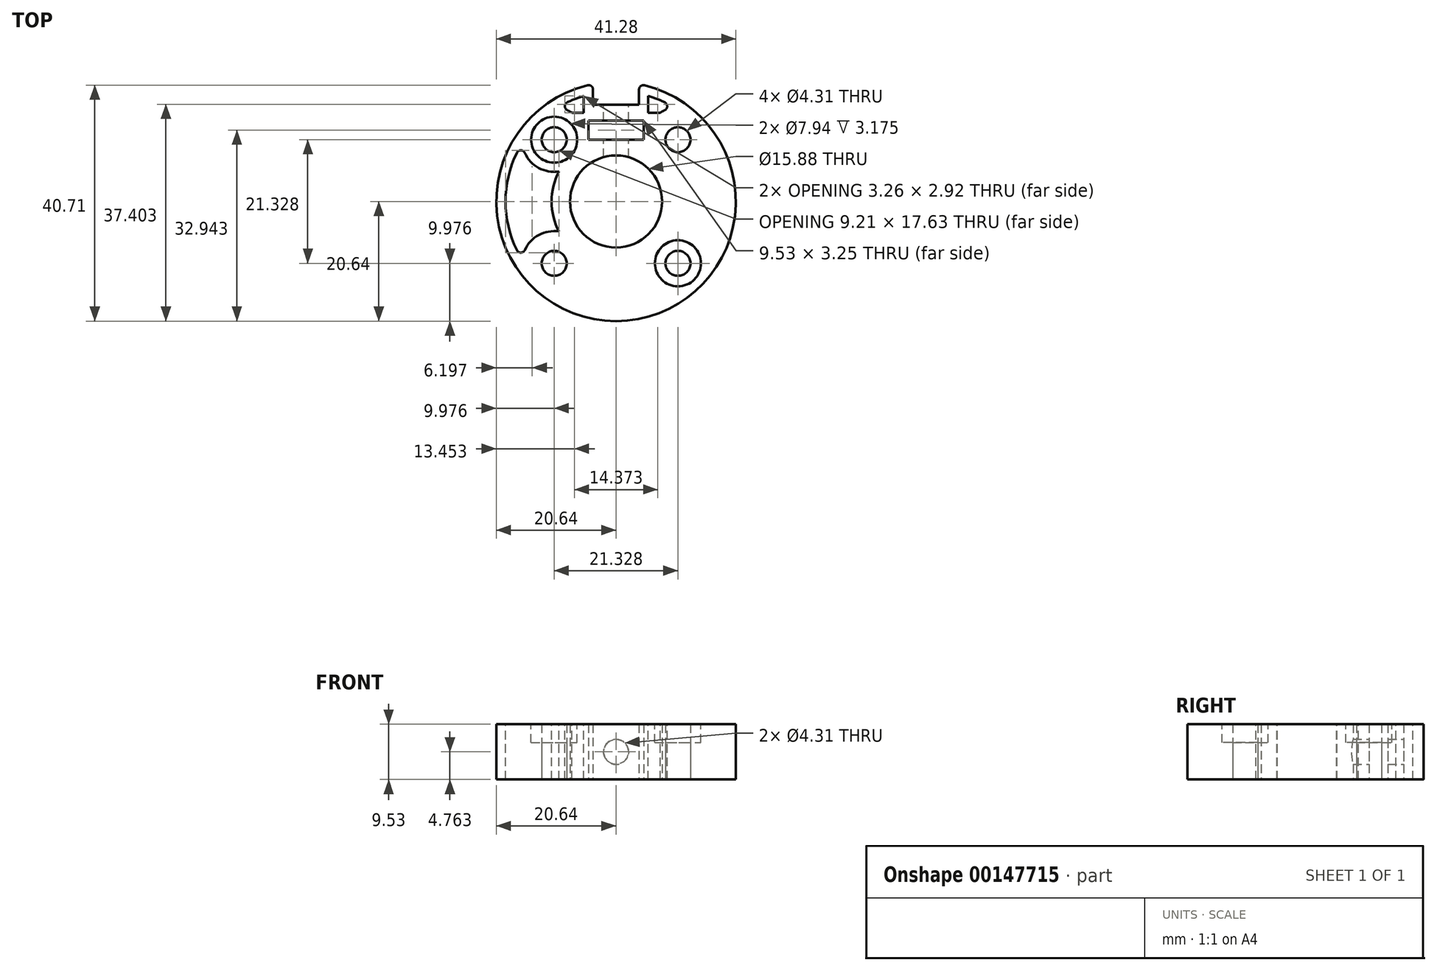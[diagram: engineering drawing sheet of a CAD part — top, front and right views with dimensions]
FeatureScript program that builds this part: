
annotation { "Feature Type Name" : "Feature", "Feature Type Description" : "" }
export const myFeature = defineFeature(function(context is Context, id is Id, definition is map)
    precondition{}
    {
        {
            var Q0;
            Q0=qCreatedBy(makeId("Top.planeOp"),FACE);
            var sketch = newSketch(context, id + "F0", { "sketchPlane" : qUnion([Q0])});
            skLineSegment(sketch, "E0.bottom", {"start": v(10.66, 10.66) * mm, "end": v(-10.66, 10.66) * mm, "construction": true});
            skLineSegment(sketch, "E0.top", {"start": v(10.66, -10.66) * mm, "end": v(-10.66, -10.66) * mm, "construction": true});
            skLineSegment(sketch, "E0.left", {"start": v(10.66, 10.66) * mm, "end": v(10.66, -10.66) * mm, "construction": true});
            skLineSegment(sketch, "E0.right", {"start": v(-10.66, 10.66) * mm, "end": v(-10.66, -10.66) * mm, "construction": true});
            skPoint(sketch, "E0.middle", {"position": v(0, 0) * mm});
            skCircle(sketch, "E1", {"center": v(-10.66, 10.66) * mm, "radius": 5.56 * mm, "construction": true});
            skLineSegment(sketch, "E2", {"start": v(0, 13.93) * mm, "end": v(0, 16.67) * mm});
            skLineSegment(sketch, "E3.bottom", {"start": v(-3.97, 20.25) * mm, "end": v(3.97, 20.25) * mm, "construction": true});
            skLineSegment(sketch, "E3.top", {"start": v(-3.97, 16.67) * mm, "end": v(3.97, 16.67) * mm});
            skLineSegment(sketch, "E3.left", {"start": v(-3.97, 20.25) * mm, "end": v(-3.97, 16.67) * mm});
            skLineSegment(sketch, "E3.right", {"start": v(3.97, 20.25) * mm, "end": v(3.97, 16.67) * mm});
            skArc(sketch, "E4", {"start": v(-3.97, 20.25) * mm, "mid": v(0, -20.64) * mm, "end": v(3.97, 20.25) * mm});
            skCircle(sketch, "E5", {"center": v(-10.66, 10.66) * mm, "radius": 2.15 * mm});
            skCircle(sketch, "E6", {"center": v(-10.66, -10.66) * mm, "radius": 2.15 * mm});
            skCircle(sketch, "E7", {"center": v(10.66, -10.66) * mm, "radius": 2.15 * mm});
            skCircle(sketch, "E8", {"center": v(10.66, 10.66) * mm, "radius": 2.15 * mm});
            skLineSegment(sketch, "E9.bottom", {"start": v(-4.76, 13.93) * mm, "end": v(4.76, 13.93) * mm});
            skLineSegment(sketch, "E9.top", {"start": v(-4.76, 10.68) * mm, "end": v(4.76, 10.68) * mm});
            skLineSegment(sketch, "E9.left", {"start": v(-4.76, 13.93) * mm, "end": v(-4.76, 10.68) * mm});
            skLineSegment(sketch, "E9.right", {"start": v(4.76, 13.93) * mm, "end": v(4.76, 10.68) * mm});
            skCircle(sketch, "E10", {"center": v(0, 0) * mm, "radius": 7.94 * mm});
            skCircle(sketch, "E11", {"center": v(0, 0) * mm, "radius": 9.53 * mm, "construction": true});
            skLineSegment(sketch, "E12", {"start": v(0, 0) * mm, "end": v(0, 7.14) * mm, "construction": true});
            skLineSegment(sketch, "E13", {"start": v(0, 7.14) * mm, "end": v(0, 7.94) * mm, "construction": true});
            skLineSegment(sketch, "E14", {"start": v(0, 7.94) * mm, "end": v(0, 10.68) * mm, "construction": true});
            skSolve(sketch);
        }
        {
            var Q0;
            Q0=qSketchRegion(id+"F0",true);
            extrude(context, id + "F1", {"entities" : qUnion([Q0]), "depth" : 9.52 * mm});
        }
        {
            var Q0;
            Q0=makeQuery(id+"F1.opExtrude","SWEPT_FACE",FACE,{"disambiguationData":[OSD([sQuery(id+"F0.wireOp",EDGE,"E3.top")])]});
            var sketch = newSketch(context, id + "F2", { "sketchPlane" : qUnion([Q0])});
            skLineSegment(sketch, "E15", {"start": v(0, 9.53) * mm, "end": v(0, 0) * mm, "construction": true});
            skCircle(sketch, "E16", {"center": v(0, 4.76) * mm, "radius": 2.15 * mm});
            skSolve(sketch);
        }
        {
            var Q0;
            Q0=qSketchRegion(id+"F2",true);
            var Q1;
            Q1=makeQuery(id+"F1.opExtrude","SWEPT_FACE",FACE,{"disambiguationData":[OSD([sQuery(id+"F0.wireOp",EDGE,"E10")])]});
            extrude(context, id + "F3", {"entities" : qUnion([Q0]), "operationType" : NewBodyOperationType.REMOVE, "endBound" : BoundingType.UP_TO_SURFACE, "oppositeDirection" : true, "endBoundEntityFace" : qUnion([Q1]), "depth" : 25.4 * mm});
        }
        {
            var Q0;
            Q0=makeQuery(id+"F1.opExtrude","CAP_FACE",FACE,{"disambiguationData":[OSD([sQuery(id+"F0.wireOp",EDGE,"zcYoioO2-fyPR-UuhC-Hgss-rbXFzuCLLck7"),sQuery(id+"F0.wireOp",EDGE,"E3.top"),sQuery(id+"F0.wireOp",EDGE,"E3.left"),sQuery(id+"F0.wireOp",EDGE,"E3.right"),sQuery(id+"F0.wireOp",EDGE,"E4"),sQuery(id+"F0.wireOp",EDGE,"E5"),sQuery(id+"F0.wireOp",EDGE,"E6"),sQuery(id+"F0.wireOp",EDGE,"E7"),sQuery(id+"F0.wireOp",EDGE,"E8")])],"isStart":true});
            cPlane(context, id + "F4", {"entities" : qUnion([Q0]), "cplaneType" : CPlaneType.OFFSET, "offset" : 6.35 * mm, "oppositeDirection" : true, "width" : 152.4 * mm, "height" : 152.4 * mm});
        }
        {
            var Q0;
            Q0=makeQuery(id+"F1.opExtrude","CAP_FACE",FACE,{"disambiguationData":[OSD([sQuery(id+"F0.wireOp",EDGE,"zcYoioO2-fyPR-UuhC-Hgss-rbXFzuCLLck7"),sQuery(id+"F0.wireOp",EDGE,"E3.top"),sQuery(id+"F0.wireOp",EDGE,"E3.left"),sQuery(id+"F0.wireOp",EDGE,"E3.right"),sQuery(id+"F0.wireOp",EDGE,"E4"),sQuery(id+"F0.wireOp",EDGE,"E5"),sQuery(id+"F0.wireOp",EDGE,"E6"),sQuery(id+"F0.wireOp",EDGE,"E7"),sQuery(id+"F0.wireOp",EDGE,"E8")])],"isStart":false});
            var sketch = newSketch(context, id + "F5", { "sketchPlane" : qUnion([Q0])});
            skCircle(sketch, "E17", {"center": v(-10.66, 10.66) * mm, "radius": 3.97 * mm});
            skCircle(sketch, "E18", {"center": v(10.66, -10.66) * mm, "radius": 3.97 * mm});
            skSolve(sketch);
        }
        {
            var Q0;
            Q0=qSketchRegion(id+"F5",true);
            var Q1;
            Q1=qCreatedBy(id+"F4.planeOp",FACE);
            extrude(context, id + "F6", {"entities" : qUnion([Q0]), "operationType" : NewBodyOperationType.REMOVE, "endBound" : BoundingType.UP_TO_SURFACE, "oppositeDirection" : true, "endBoundEntityFace" : qUnion([Q1]), "depth" : 25.4 * mm});
        }
        {
            var Q0;
            Q0=makeQuery(id+"F1.opExtrude","CAP_FACE",FACE,{"disambiguationData":[OSD([sQuery(id+"F0.wireOp",EDGE,"zcYoioO2-fyPR-UuhC-Hgss-rbXFzuCLLck7"),sQuery(id+"F0.wireOp",EDGE,"E3.top"),sQuery(id+"F0.wireOp",EDGE,"E3.left"),sQuery(id+"F0.wireOp",EDGE,"E3.right"),sQuery(id+"F0.wireOp",EDGE,"E4"),sQuery(id+"F0.wireOp",EDGE,"E5"),sQuery(id+"F0.wireOp",EDGE,"E6"),sQuery(id+"F0.wireOp",EDGE,"E7"),sQuery(id+"F0.wireOp",EDGE,"E8")])],"isStart":false});
            var sketch = newSketch(context, id + "F7", { "sketchPlane" : qUnion([Q0])});
            skArc(sketch, "E19", {"start": v(-16.19, 10.05) * mm, "mid": v(-14.05, 6.26) * mm, "end": v(-9.84, 5.17) * mm});
            skArc(sketch, "E20", {"start": v(-16.19, 10.05) * mm, "mid": v(-19.05, 0) * mm, "end": v(-16.19, -10.05) * mm});
            skArc(sketch, "E21", {"start": v(-9.84, -5.17) * mm, "mid": v(-14.05, -6.26) * mm, "end": v(-16.19, -10.05) * mm});
            skArc(sketch, "E22", {"start": v(-9.84, 5.17) * mm, "mid": v(-11.11, 0) * mm, "end": v(-9.84, -5.17) * mm});
            skSolve(sketch);
        }
        {
            var Q0;
            Q0=qSketchRegion(id+"F7",true);
            var Q1;
            Q1=makeQuery(id+"F1.opExtrude","CAP_FACE",FACE,{"disambiguationData":[OSD([sQuery(id+"F0.wireOp",EDGE,"zcYoioO2-fyPR-UuhC-Hgss-rbXFzuCLLck7"),sQuery(id+"F0.wireOp",EDGE,"E3.top"),sQuery(id+"F0.wireOp",EDGE,"E3.left"),sQuery(id+"F0.wireOp",EDGE,"E3.right"),sQuery(id+"F0.wireOp",EDGE,"E4"),sQuery(id+"F0.wireOp",EDGE,"E5"),sQuery(id+"F0.wireOp",EDGE,"E6"),sQuery(id+"F0.wireOp",EDGE,"E7"),sQuery(id+"F0.wireOp",EDGE,"E8")])],"isStart":true});
            extrude(context, id + "F8", {"entities" : qUnion([Q0]), "operationType" : NewBodyOperationType.REMOVE, "endBound" : BoundingType.UP_TO_SURFACE, "oppositeDirection" : true, "endBoundEntityFace" : qUnion([Q1]), "depth" : 25.4 * mm});
        }
        {
            var Q0;
            Q0=makeQuery(id+"F1.opExtrude","SWEPT_FACE",FACE,{"disambiguationData":[OSD([sQuery(id+"F0.wireOp",EDGE,"E3.top")])]});
            var sketch = newSketch(context, id + "F9", { "sketchPlane" : qUnion([Q0])});
            skLineSegment(sketch, "E23", {"start": v(0, 0) * mm, "end": v(0, 9.53) * mm, "construction": true});
            skCircle(sketch, "E24", {"center": v(0, 4.76) * mm, "radius": 2.15 * mm});
            skSolve(sketch);
        }
        {
            var Q0;
            Q0=qSketchRegion(id+"F9",true);
            var Q1;
            Q1=makeQuery(id+"F1.opExtrude","SWEPT_FACE",FACE,{"disambiguationData":[OSD([sQuery(id+"F0.wireOp",EDGE,"E10")])]});
            extrude(context, id + "F10", {"entities" : qUnion([Q0]), "operationType" : NewBodyOperationType.REMOVE, "endBound" : BoundingType.UP_TO_SURFACE, "oppositeDirection" : true, "endBoundEntityFace" : qUnion([Q1]), "depth" : 25.4 * mm});
        }
        {
            var Q0;
            Q0=makeQuery(id+"F1.opExtrude","CAP_FACE",FACE,{"disambiguationData":[OSD([sQuery(id+"F0.wireOp",EDGE,"E3.top"),sQuery(id+"F0.wireOp",EDGE,"E3.left"),sQuery(id+"F0.wireOp",EDGE,"E3.right"),sQuery(id+"F0.wireOp",EDGE,"E4"),sQuery(id+"F0.wireOp",EDGE,"E5"),sQuery(id+"F0.wireOp",EDGE,"E6"),sQuery(id+"F0.wireOp",EDGE,"E7"),sQuery(id+"F0.wireOp",EDGE,"E8"),sQuery(id+"F0.wireOp",EDGE,"E9.bottom"),sQuery(id+"F0.wireOp",EDGE,"E9.top"),sQuery(id+"F0.wireOp",EDGE,"E9.left"),sQuery(id+"F0.wireOp",EDGE,"E9.right"),sQuery(id+"F0.wireOp",EDGE,"E10")])],"isStart":false});
            var sketch = newSketch(context, id + "F11", { "sketchPlane" : qUnion([Q0])});
            skArc(sketch, "E25", {"start": v(-7.6, 15.3) * mm, "mid": v(-8.77, 15.89) * mm, "end": v(-10.05, 16.19) * mm});
            skArc(sketch, "E26", {"start": v(-5.56, 18.22) * mm, "mid": v(-7.87, 17.35) * mm, "end": v(-10.05, 16.19) * mm});
            skLineSegment(sketch, "E27", {"start": v(-5.56, 18.22) * mm, "end": v(-5.56, 15.3) * mm});
            skLineSegment(sketch, "E28", {"start": v(-5.56, 15.3) * mm, "end": v(-7.6, 15.3) * mm});
            skCircle(sketch, "E29", {"center": v(-4.76, 13.93) * mm, "radius": 1.59 * mm, "construction": true});
            skLineSegment(sketch, "E30", {"start": v(5.56, 18.22) * mm, "end": v(5.56, 15.3) * mm});
            skLineSegment(sketch, "E31", {"start": v(5.56, 15.3) * mm, "end": v(7.6, 15.3) * mm});
            skArc(sketch, "E32", {"start": v(10.05, 16.19) * mm, "mid": v(7.87, 17.35) * mm, "end": v(5.56, 18.22) * mm});
            skArc(sketch, "E33", {"start": v(10.05, 16.19) * mm, "mid": v(8.77, 15.89) * mm, "end": v(7.6, 15.3) * mm});
            skSolve(sketch);
        }
        {
            var Q0;
            Q0=qSketchRegion(id+"F11",true);
            var Q1;
            Q1=makeQuery(id+"F1.opExtrude","CAP_FACE",FACE,{"disambiguationData":[OSD([sQuery(id+"F0.wireOp",EDGE,"E3.top"),sQuery(id+"F0.wireOp",EDGE,"E3.left"),sQuery(id+"F0.wireOp",EDGE,"E3.right"),sQuery(id+"F0.wireOp",EDGE,"E4"),sQuery(id+"F0.wireOp",EDGE,"E5"),sQuery(id+"F0.wireOp",EDGE,"E6"),sQuery(id+"F0.wireOp",EDGE,"E7"),sQuery(id+"F0.wireOp",EDGE,"E8"),sQuery(id+"F0.wireOp",EDGE,"E9.bottom"),sQuery(id+"F0.wireOp",EDGE,"E9.top"),sQuery(id+"F0.wireOp",EDGE,"E9.left"),sQuery(id+"F0.wireOp",EDGE,"E9.right"),sQuery(id+"F0.wireOp",EDGE,"E10")])],"isStart":true});
            extrude(context, id + "F12", {"entities" : qUnion([Q0]), "operationType" : NewBodyOperationType.REMOVE, "endBound" : BoundingType.UP_TO_SURFACE, "oppositeDirection" : true, "endBoundEntityFace" : qUnion([Q1]), "depth" : 25.4 * mm});
        }
        {
            var Q0;
            Q0=makeQuery(id+"F8.boolean.opBoolean","COPY",EDGE,{"derivedFrom":makeQuery(id+"F8.opExtrude","SWEPT_EDGE",EDGE,{"disambiguationData":[OSD([sQuery(id+"F7.wireOp",EDGE,"E20"),sQuery(id+"F7.wireOp",EDGE,"E21")])]})});
            var Q1;
            Q1=makeQuery(id+"FlX28BifZiOdl7F_1.1.F8.boolean.opBoolean","COPY",EDGE,{"derivedFrom":makeQuery(id+"FlX28BifZiOdl7F_1.1.F8.opExtrude","SWEPT_EDGE",EDGE,{"disambiguationData":[OSD([sQuery(id+"F7.wireOp",EDGE,"E19"),sQuery(id+"F7.wireOp",EDGE,"E20")])]})});
            var Q2;
            Q2=makeQuery(id+"F8.boolean.opBoolean","COPY",EDGE,{"derivedFrom":makeQuery(id+"F8.opExtrude","SWEPT_EDGE",EDGE,{"disambiguationData":[OSD([sQuery(id+"F7.wireOp",EDGE,"E19"),sQuery(id+"F7.wireOp",EDGE,"E20")])]})});
            var Q3;
            Q3=makeQuery(id+"FlX28BifZiOdl7F_1.1.F8.boolean.opBoolean","COPY",EDGE,{"derivedFrom":makeQuery(id+"FlX28BifZiOdl7F_1.1.F8.opExtrude","SWEPT_EDGE",EDGE,{"disambiguationData":[OSD([sQuery(id+"F7.wireOp",EDGE,"E20"),sQuery(id+"F7.wireOp",EDGE,"E21")])]})});
            var Q4;
            Q4=makeQuery(id+"FlX28BifZiOdl7F_1.2.F8.boolean.opBoolean","COPY",EDGE,{"derivedFrom":makeQuery(id+"FlX28BifZiOdl7F_1.2.F8.opExtrude","SWEPT_EDGE",EDGE,{"disambiguationData":[OSD([sQuery(id+"F7.wireOp",EDGE,"E19"),sQuery(id+"F7.wireOp",EDGE,"E20")])]})});
            var Q5;
            Q5=makeQuery(id+"FlX28BifZiOdl7F_1.2.F8.boolean.opBoolean","COPY",EDGE,{"derivedFrom":makeQuery(id+"FlX28BifZiOdl7F_1.2.F8.opExtrude","SWEPT_EDGE",EDGE,{"disambiguationData":[OSD([sQuery(id+"F7.wireOp",EDGE,"E20"),sQuery(id+"F7.wireOp",EDGE,"E21")])]})});
            var Q6;
            Q6=makeQuery(id+"F12.boolean.opBoolean","COPY",EDGE,{"derivedFrom":makeQuery(id+"F12.opExtrude","SWEPT_EDGE",EDGE,{"disambiguationData":[OSD([sQuery(id+"F11.wireOp",EDGE,"E32"),sQuery(id+"F11.wireOp",EDGE,"E33")])]})});
            var Q7;
            Q7=makeQuery(id+"F1.opExtrude","SWEPT_EDGE",EDGE,{"disambiguationData":[OSD([sQuery(id+"F0.wireOp",EDGE,"E3.right"),sQuery(id+"F0.wireOp",EDGE,"E4")])]});
            var Q8;
            Q8=makeQuery(id+"F1.opExtrude","SWEPT_EDGE",EDGE,{"disambiguationData":[OSD([sQuery(id+"F0.wireOp",EDGE,"E3.left"),sQuery(id+"F0.wireOp",EDGE,"E4")])]});
            var Q9;
            Q9=makeQuery(id+"F12.boolean.opBoolean","COPY",EDGE,{"derivedFrom":makeQuery(id+"F12.opExtrude","SWEPT_EDGE",EDGE,{"disambiguationData":[OSD([sQuery(id+"F11.wireOp",EDGE,"E25"),sQuery(id+"F11.wireOp",EDGE,"E26")])]})});
            fillet(context, id + "F13", {"entities" : qUnion([Q0, Q1, Q2, Q3, Q4, Q5, Q6, Q7, Q8, Q9]), "radius" : 0.76 * mm, "tangentPropagation" : true, "allowEdgeOverflow" : false});
        }
    });
